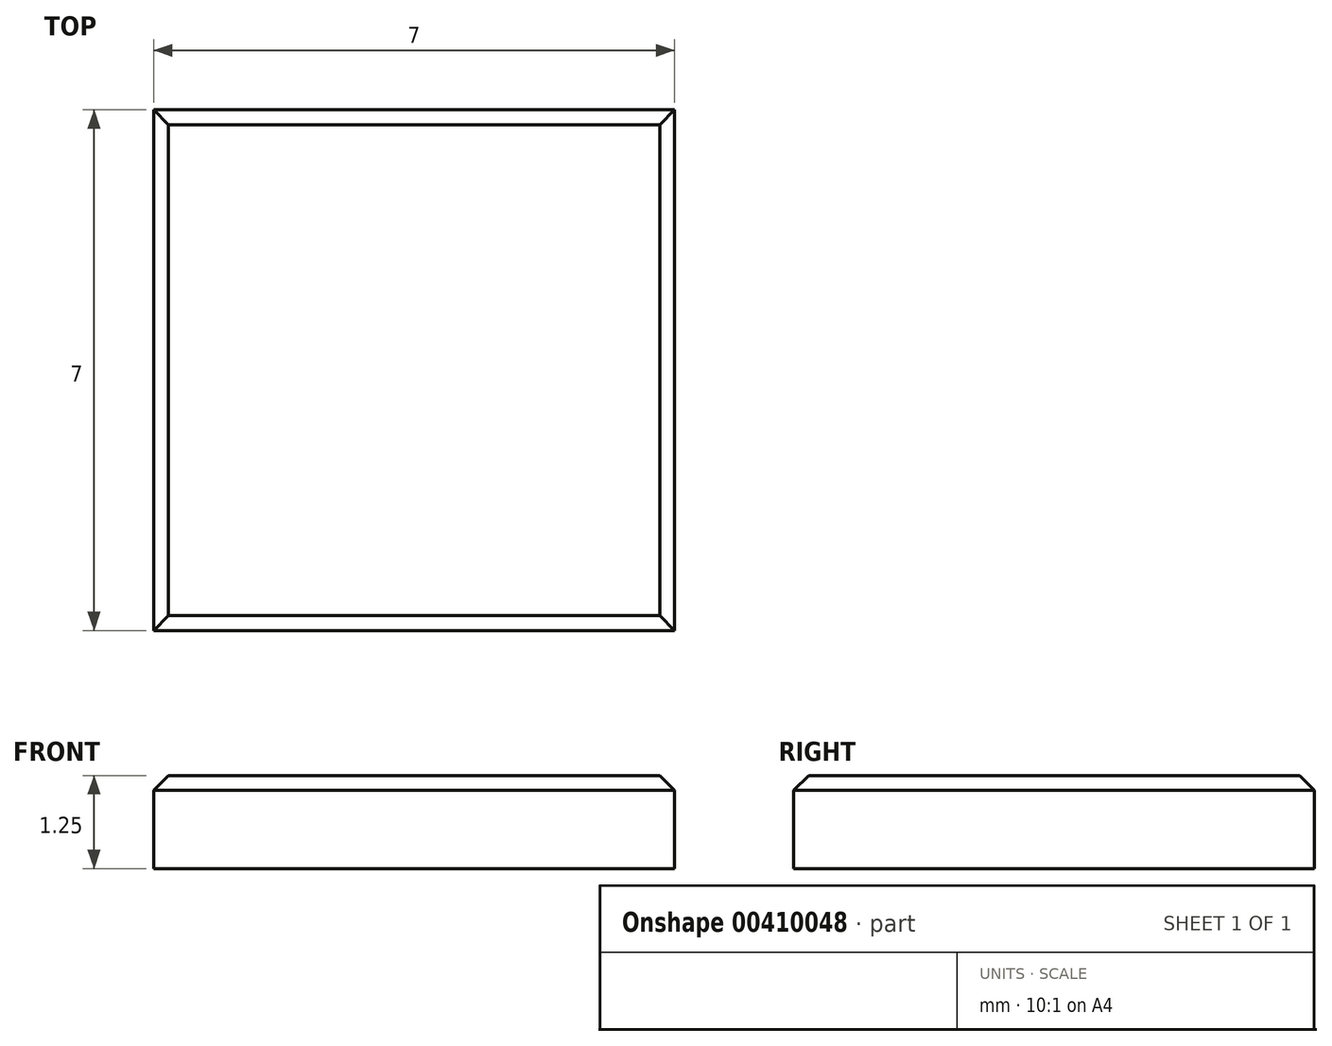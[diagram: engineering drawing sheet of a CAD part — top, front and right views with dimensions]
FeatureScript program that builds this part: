
annotation { "Feature Type Name" : "Feature", "Feature Type Description" : "" }
export const myFeature = defineFeature(function(context is Context, id is Id, definition is map)
    precondition{}
    {
        {
            var Q0;
            Q0=qCreatedBy(makeId("Top.planeOp"),FACE);
            var sketch = newSketch(context, id + "F0", { "sketchPlane" : qUnion([Q0])});
            skLineSegment(sketch, "E0.bottom", {"start": v(0, 0) * mm, "end": v(7, 0) * mm});
            skLineSegment(sketch, "E0.top", {"start": v(0, 7) * mm, "end": v(7, 7) * mm});
            skLineSegment(sketch, "E0.left", {"start": v(0, 0) * mm, "end": v(0, 7) * mm});
            skLineSegment(sketch, "E0.right", {"start": v(7, 0) * mm, "end": v(7, 7) * mm});
            skSolve(sketch);
        }
        {
            var Q0;
            Q0 = qSketchRegion(id + "F0", true);
            extrude(context, id + "F1", {"entities" : qUnion([Q0]), "depth" : 1.25 * mm});
        }
        {
            var Q0;
            Q0=makeQuery(id+"F1.opExtrude","CAP_EDGE",EDGE,{"disambiguationData":[OSD([sQuery(id+"F0.wireOp",EDGE,"E0.bottom")])],"isStart":false});
            var Q1;
            Q1=makeQuery(id+"F1.opExtrude","CAP_EDGE",EDGE,{"disambiguationData":[OSD([sQuery(id+"F0.wireOp",EDGE,"E0.left")])],"isStart":false});
            var Q2;
            Q2=makeQuery(id+"F1.opExtrude","CAP_EDGE",EDGE,{"disambiguationData":[OSD([sQuery(id+"F0.wireOp",EDGE,"E0.top")])],"isStart":false});
            var Q3;
            Q3=makeQuery(id+"F1.opExtrude","CAP_EDGE",EDGE,{"disambiguationData":[OSD([sQuery(id+"F0.wireOp",EDGE,"E0.right")])],"isStart":false});
            chamfer(context, id + "F2", {"entities" : qUnion([Q0, Q1, Q2, Q3]), "width" : 0.2 * mm, "tangentPropagation" : true});
        }
    });
